# Revit family: Sanitary_Accessories_AXOR_42830CHN-AXOR-Universal-Softsquare-Rail_new
name_source: partatom
category: Furniture
revit_build: Autodesk Revit 2018 (Build: 20170223_1515(x64)
units: mm (PartAtom-declared; Revit-internal decimal feet)

## family parameters
Always vertical = No
Cut with Voids When Loaded = No
OmniClass Number = 23.31.25.25
OmniClass Title = Towel Bars
Room Calculation Point = No
Shared = No
Work Plane-Based = Yes

## types (4) — shared parameters
Always visible = Yes
BIMobject category = Accessories
Default Elevation = 1219.2 mm  [stored 4 ft]
Description = AXOR Universal Softsquare Rail grab bar 300 mm
Design country = Germany
EAN code = 4059625428504
Edition number = 1
IFC Classification = Furnishing Element
Manufacturer = AXOR
Manufacturer country = Germany
Manufacturer name = AXOR
Material main = Metal
Material secondary = Chrome
Model = 42830CHN
OmniClass Code = 23-31 25 25
OmniClass Description = Towel Bars
Product Guid = 697d6b8e-dfa8-484d-b70a-aa27930929aa
Product SKU = 42830CHN
Product data url = https://bimobject.com
Product family = AXOR Universal Softsquare
Product group = Grab bars
Product name = 42830CHN AXOR Universal Softsquare Rail grab bar 300 mm
QR code = https://bimobject.com
URL = https://www.axor-design.com
Weight Net (Kg) = 1.5

## per-type parameters (varying)
| type | Material 1 |
| 007 Chrome | AXOR - Metal - 007 Chrome |
| 347 Brushed Black Chrome | AXOR - Metal - 347 Brushed Black Chrome |
| 677 Matt Black | AXOR - Metal - 677 Matt Black |
| 997 Polished Gold Optic | AXOR - Metal - 997 Polished Gold Optic |

note: [stored X ft] marks values corroborated as IEEE doubles in the binary element streams (Revit-internal decimal feet)

## geometry (parser evidence)
native form markers: Sweep x3
no freeform markers — native parametric forms only
